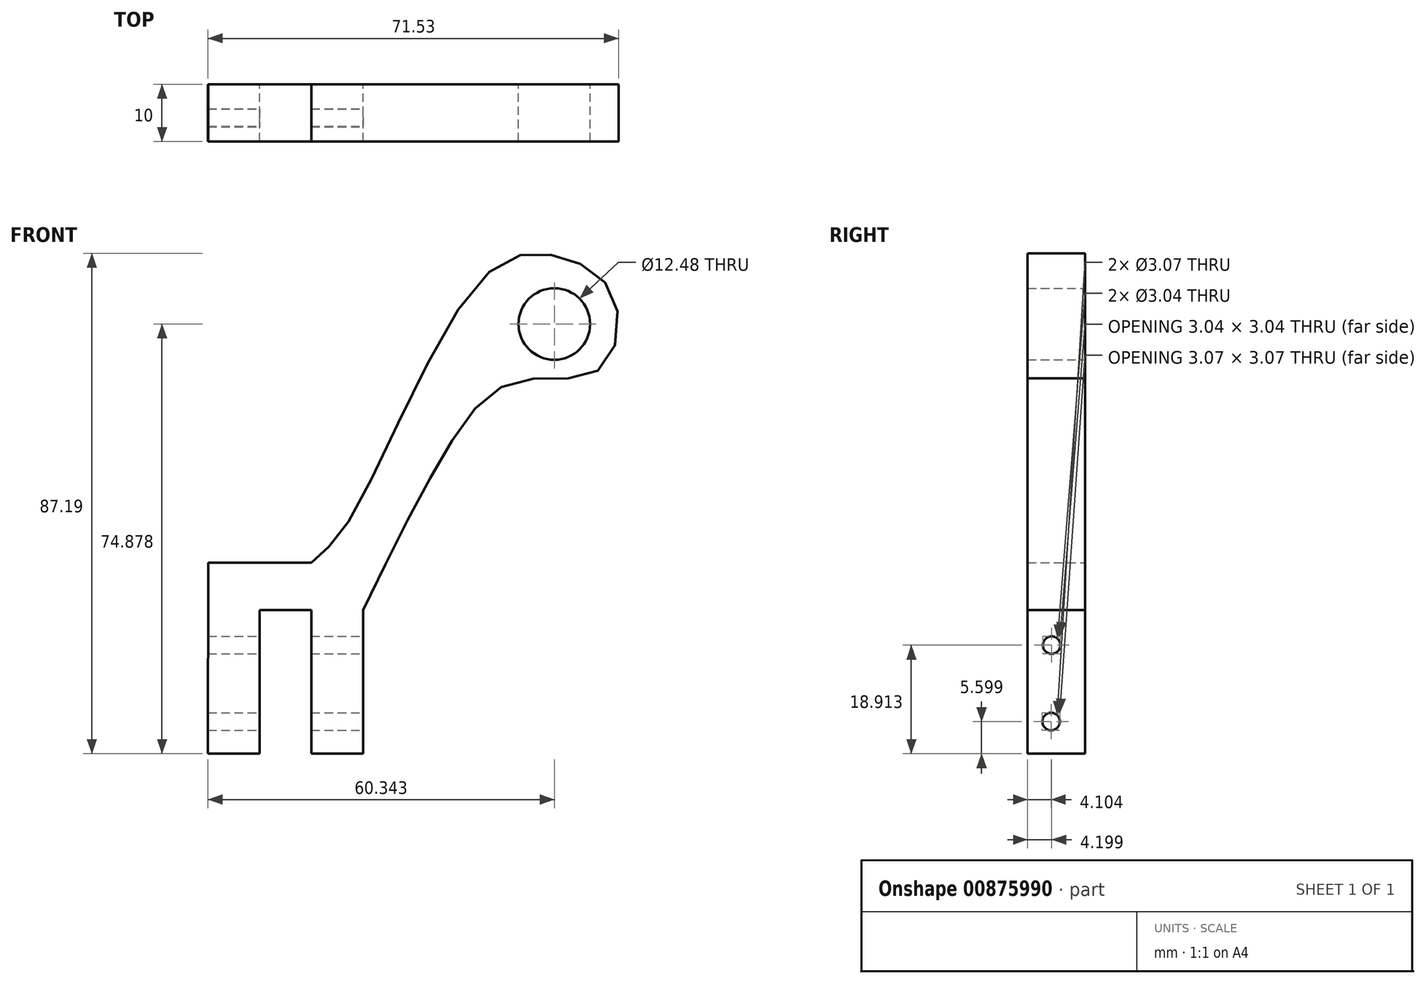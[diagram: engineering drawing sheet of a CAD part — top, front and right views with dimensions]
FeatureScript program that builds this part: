
annotation { "Feature Type Name" : "Feature", "Feature Type Description" : "" }
export const myFeature = defineFeature(function(context is Context, id is Id, definition is map)
    precondition{}
    {
        {
            var Q0;
            Q0=qCreatedBy(makeId("Front.planeOp"),FACE);
            var sketch = newSketch(context, id + "F0", { "sketchPlane" : qUnion([Q0])});
            skLineSegment(sketch, "E0", {"start": v(-48.02, -25) * mm, "end": v(-39.02, -25) * mm});
            skLineSegment(sketch, "E1", {"start": v(-39.02, -25) * mm, "end": v(-39.02, 0) * mm});
            skLineSegment(sketch, "E2", {"start": v(-39.02, 0) * mm, "end": v(-30.02, 0) * mm});
            skLineSegment(sketch, "E3", {"start": v(-30.02, 0) * mm, "end": v(-30.02, -25) * mm});
            skLineSegment(sketch, "E4", {"start": v(-30.02, -25) * mm, "end": v(-21.02, -25) * mm});
            skLineSegment(sketch, "E5", {"start": v(-21.02, -25) * mm, "end": v(-21.02, 0) * mm});
            skLineSegment(sketch, "E6", {"start": v(-30.02, 8.3) * mm, "end": v(-48, 8.3) * mm});
            skLineSegment(sketch, "E7", {"start": v(-48, 8.3) * mm, "end": v(-48.02, -25) * mm});
            skPoint(sketch, "E8", {"position": v(-21.02, 6.98) * mm});
            skCircle(sketch, "E9", {"center": v(12.32, 49.88) * mm, "radius": 6.24 * mm});
            skFitSpline(sketch, "E10", {"points": [v(-30.02, 8.3) * mm, v(-22.58, 17.08) * mm, v(0, 58.05) * mm, v(13.12, 61.66) * mm, v(22.77, 54.4) * mm, v(20, 41.8) * mm, v(5.68, 39.93) * mm, v(-6.49, 27.93) * mm, v(-21.02, 0) * mm], "startDerivative": vector(69.1, 57.91) * mm, "endDerivative": vector(-89.8, -184.08) * mm});
            skSolve(sketch);
        }
        {
            var Q0;
            Q0 = qSketchRegion(id + "F0", true);
            extrude(context, id + "F1", {"entities" : qUnion([Q0]), "depth" : 10 * mm, "offsetDistance" : 25 * mm});
        }
        {
            var Q0;
            Q0=qCreatedBy(makeId("Right.planeOp"),FACE);
            var sketch = newSketch(context, id + "F2", { "sketchPlane" : qUnion([Q0])});
            skCircle(sketch, "E11", {"center": v(-5.8, -6.09) * mm, "radius": 1.52 * mm});
            skCircle(sketch, "E12", {"center": v(-5.9, -19.4) * mm, "radius": 1.53 * mm});
            skSolve(sketch);
        }
        {
            var Q0;
            Q0 = qSketchRegion(id + "F2", true);
            extrude(context, id + "F3", {"entities" : qUnion([Q0]), "operationType" : NewBodyOperationType.REMOVE, "oppositeDirection" : true, "depth" : 88 * mm, "offsetDistance" : 25 * mm});
        }
    });
